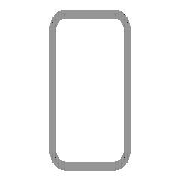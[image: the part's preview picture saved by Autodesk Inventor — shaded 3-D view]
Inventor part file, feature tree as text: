
AUTODESK INVENTOR PART (.ipt)
format: ipt  version: 2025 (Build 290162010, 162A)  size: 141,312 bytes
history: native  units: mm (DEFAULTED — no unit token found)
features: other x4, sketch x1, plane x1
ambient origin geometry x8: Origin, YZ Plane, XZ Plane, XY Plane, X Axis, Y Axis, Z Axis, Center Point
bodies: Solid1 (feature_tree), Body (feature_tree)
feature tree (6):
  parser-record x1  (decoder bookkeeping rows leaked as tree rows — omitted from the tree; the rows remain in map.json)
  other  "Driven Length"
  other  "Start Plane"
  other  "End Plane"
  sketch  "Sketch3"  dims[d3=1940.0mm d4=0.0mm d7=6.0mm d9=40.0mm d11=60.0mm d12=3.0mm d13=-0.0mm d14=1940.0mm d15=20.0mm d16=30.0mm d17=90.0deg d18=1940.0mm]
  plane  "Work Plane3"
